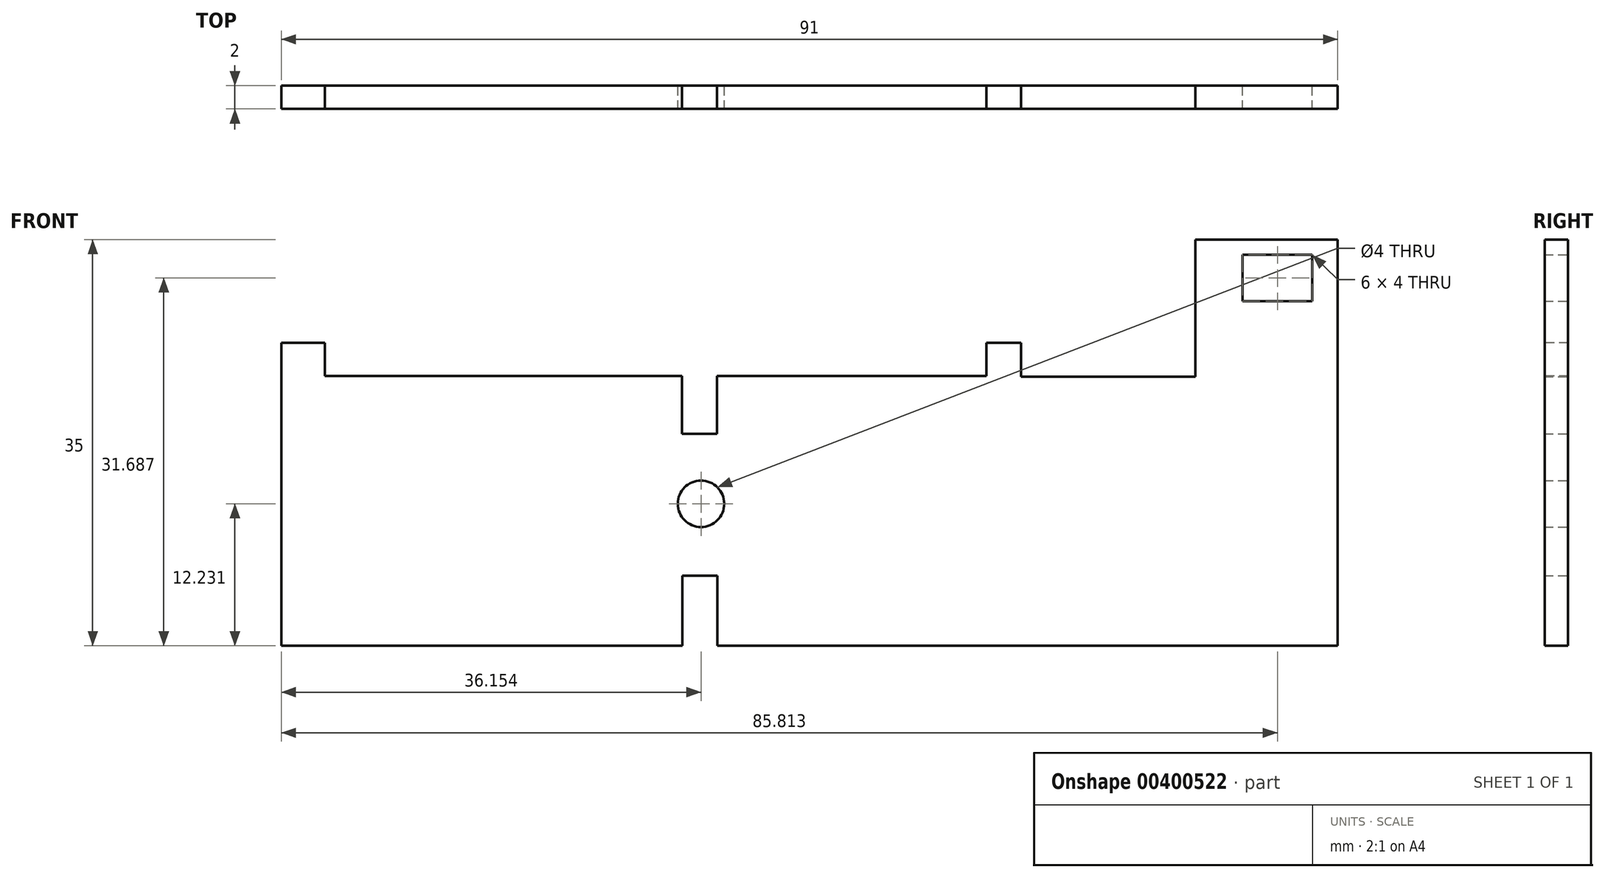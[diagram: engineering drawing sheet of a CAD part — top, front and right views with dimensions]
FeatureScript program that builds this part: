
annotation { "Feature Type Name" : "Feature", "Feature Type Description" : "" }
export const myFeature = defineFeature(function(context is Context, id is Id, definition is map)
    precondition{}
    {
        {
            var Q0;
            Q0=qCreatedBy(makeId("Front.planeOp"),FACE);
            var sketch = newSketch(context, id + "F0", { "sketchPlane" : qUnion([Q0])});
            skLineSegment(sketch, "E0.bottom", {"start": v(-63.74, 27.78) * mm, "end": v(27.26, 27.78) * mm});
            skLineSegment(sketch, "E0.top", {"start": v(-63.74, -7.22) * mm, "end": v(27.26, -7.22) * mm});
            skLineSegment(sketch, "E0.left", {"start": v(-63.74, 27.78) * mm, "end": v(-63.74, -7.22) * mm});
            skLineSegment(sketch, "E0.right", {"start": v(27.26, 27.78) * mm, "end": v(27.26, -7.22) * mm});
            skSolve(sketch);
        }
        {
            var Q0;
            Q0 = qSketchRegion(id + "F0", true);
            extrude(context, id + "F1", {"entities" : qUnion([Q0]), "depth" : 2 * mm});
        }
        {
            var Q0;
            Q0=qCreatedBy(makeId("Front.planeOp"),FACE);
            var sketch = newSketch(context, id + "F2", { "sketchPlane" : qUnion([Q0])});
            skLineSegment(sketch, "E1.bottom", {"start": v(15, 27.97) * mm, "end": v(0, 27.97) * mm});
            skLineSegment(sketch, "E1.top", {"start": v(15, 15.97) * mm, "end": v(0, 15.97) * mm});
            skLineSegment(sketch, "E1.left", {"start": v(15, 27.97) * mm, "end": v(15, 15.97) * mm});
            skLineSegment(sketch, "E1.right", {"start": v(0, 27.97) * mm, "end": v(0, 15.97) * mm});
            skSolve(sketch);
        }
        {
            var Q0;
            Q0 = qSketchRegion(id + "F2", true);
            extrude(context, id + "F3", {"entities" : qUnion([Q0]), "operationType" : NewBodyOperationType.REMOVE, "depth" : 3 * mm});
        }
        {
            var Q0;
            Q0=qCreatedBy(makeId("Front.planeOp"),FACE);
            var sketch = newSketch(context, id + "F4", { "sketchPlane" : qUnion([Q0])});
            skLineSegment(sketch, "E2", {"start": v(0, 15.93) * mm, "end": v(0, 18.93) * mm});
            skLineSegment(sketch, "E3.bottom", {"start": v(0, 28.96) * mm, "end": v(-65.69, 28.96) * mm});
            skLineSegment(sketch, "E3.top", {"start": v(0, 18.9) * mm, "end": v(-65.69, 18.9) * mm});
            skLineSegment(sketch, "E3.left", {"start": v(0, 28.96) * mm, "end": v(0, 18.9) * mm});
            skLineSegment(sketch, "E3.right", {"start": v(-65.69, 28.96) * mm, "end": v(-65.69, 18.9) * mm});
            skSolve(sketch);
        }
        {
            var Q0;
            Q0 = qSketchRegion(id + "F4", true);
            extrude(context, id + "F5", {"entities" : qUnion([Q0]), "operationType" : NewBodyOperationType.REMOVE, "oppositeDirection" : true, "depth" : -5 * mm});
        }
        {
            var Q0;
            Q0=qCreatedBy(makeId("Front.planeOp"),FACE);
            var sketch = newSketch(context, id + "F6", { "sketchPlane" : qUnion([Q0])});
            skLineSegment(sketch, "E4.bottom", {"start": v(-3, 19.02) * mm, "end": v(-60, 19.02) * mm});
            skLineSegment(sketch, "E4.top", {"start": v(-3, 16.02) * mm, "end": v(-60, 16.02) * mm});
            skLineSegment(sketch, "E4.left", {"start": v(-3, 19.02) * mm, "end": v(-3, 16.02) * mm});
            skLineSegment(sketch, "E4.right", {"start": v(-60, 19.02) * mm, "end": v(-60, 16.02) * mm});
            skSolve(sketch);
        }
        {
            var Q0;
            Q0 = qSketchRegion(id + "F6", true);
            extrude(context, id + "F7", {"entities" : qUnion([Q0]), "operationType" : NewBodyOperationType.REMOVE, "oppositeDirection" : true, "depth" : -3 * mm});
        }
        {
            var Q0;
            Q0=qCreatedBy(makeId("Front.planeOp"),FACE);
            var sketch = newSketch(context, id + "F8", { "sketchPlane" : qUnion([Q0])});
            skLineSegment(sketch, "E5", {"start": v(-3.21, 16.04) * mm, "end": v(-26.21, 16.04) * mm});
            skLineSegment(sketch, "E6.bottom", {"start": v(-26.21, 16.04) * mm, "end": v(-29.21, 16.04) * mm});
            skLineSegment(sketch, "E6.top", {"start": v(-26.21, 11.04) * mm, "end": v(-29.21, 11.04) * mm});
            skLineSegment(sketch, "E6.left", {"start": v(-26.21, 16.04) * mm, "end": v(-26.21, 11.04) * mm});
            skLineSegment(sketch, "E6.right", {"start": v(-29.21, 16.04) * mm, "end": v(-29.21, 11.04) * mm});
            skSolve(sketch);
        }
        {
            var Q0;
            Q0 = qSketchRegion(id + "F8", true);
            extrude(context, id + "F9", {"entities" : qUnion([Q0]), "operationType" : NewBodyOperationType.REMOVE, "oppositeDirection" : true, "depth" : -9 * mm});
        }
        {
            var Q0;
            Q0=qCreatedBy(makeId("Front.planeOp"),FACE);
            var sketch = newSketch(context, id + "F10", { "sketchPlane" : qUnion([Q0])});
            skLineSegment(sketch, "E7.bottom", {"start": v(-26.18, -7.49) * mm, "end": v(-29.18, -7.49) * mm});
            skLineSegment(sketch, "E7.top", {"start": v(-26.18, -1.19) * mm, "end": v(-29.18, -1.19) * mm});
            skLineSegment(sketch, "E7.left", {"start": v(-26.18, -7.49) * mm, "end": v(-26.18, -1.19) * mm});
            skLineSegment(sketch, "E7.right", {"start": v(-29.18, -7.49) * mm, "end": v(-29.18, -1.19) * mm});
            skSolve(sketch);
        }
        {
            var Q0;
            Q0 = qSketchRegion(id + "F10", true);
            extrude(context, id + "F11", {"entities" : qUnion([Q0]), "operationType" : NewBodyOperationType.REMOVE, "oppositeDirection" : true, "depth" : -4 * mm});
        }
        {
            var Q0;
            Q0=qCreatedBy(makeId("Front.planeOp"),FACE);
            var sketch = newSketch(context, id + "F12", { "sketchPlane" : qUnion([Q0])});
            skCircle(sketch, "E8", {"center": v(-27.59, 5.01) * mm, "radius": 2 * mm});
            skSolve(sketch);
        }
        {
            var Q0;
            Q0 = qSketchRegion(id + "F12", true);
            extrude(context, id + "F13", {"entities" : qUnion([Q0]), "operationType" : NewBodyOperationType.REMOVE, "oppositeDirection" : true, "depth" : -4 * mm});
        }
        {
            var Q0;
            Q0=qCreatedBy(makeId("Front.planeOp"),FACE);
            var sketch = newSketch(context, id + "F14", { "sketchPlane" : qUnion([Q0])});
            skLineSegment(sketch, "E9.bottom", {"start": v(25.07, 26.47) * mm, "end": v(19.07, 26.47) * mm});
            skLineSegment(sketch, "E9.top", {"start": v(25.07, 22.47) * mm, "end": v(19.07, 22.47) * mm});
            skLineSegment(sketch, "E9.left", {"start": v(25.07, 26.47) * mm, "end": v(25.07, 22.47) * mm});
            skLineSegment(sketch, "E9.right", {"start": v(19.07, 26.47) * mm, "end": v(19.07, 22.47) * mm});
            skSolve(sketch);
        }
        {
            var Q0;
            Q0 = qSketchRegion(id + "F14", true);
            extrude(context, id + "F15", {"entities" : qUnion([Q0]), "operationType" : NewBodyOperationType.REMOVE, "oppositeDirection" : true, "depth" : -4 * mm});
        }
    });
